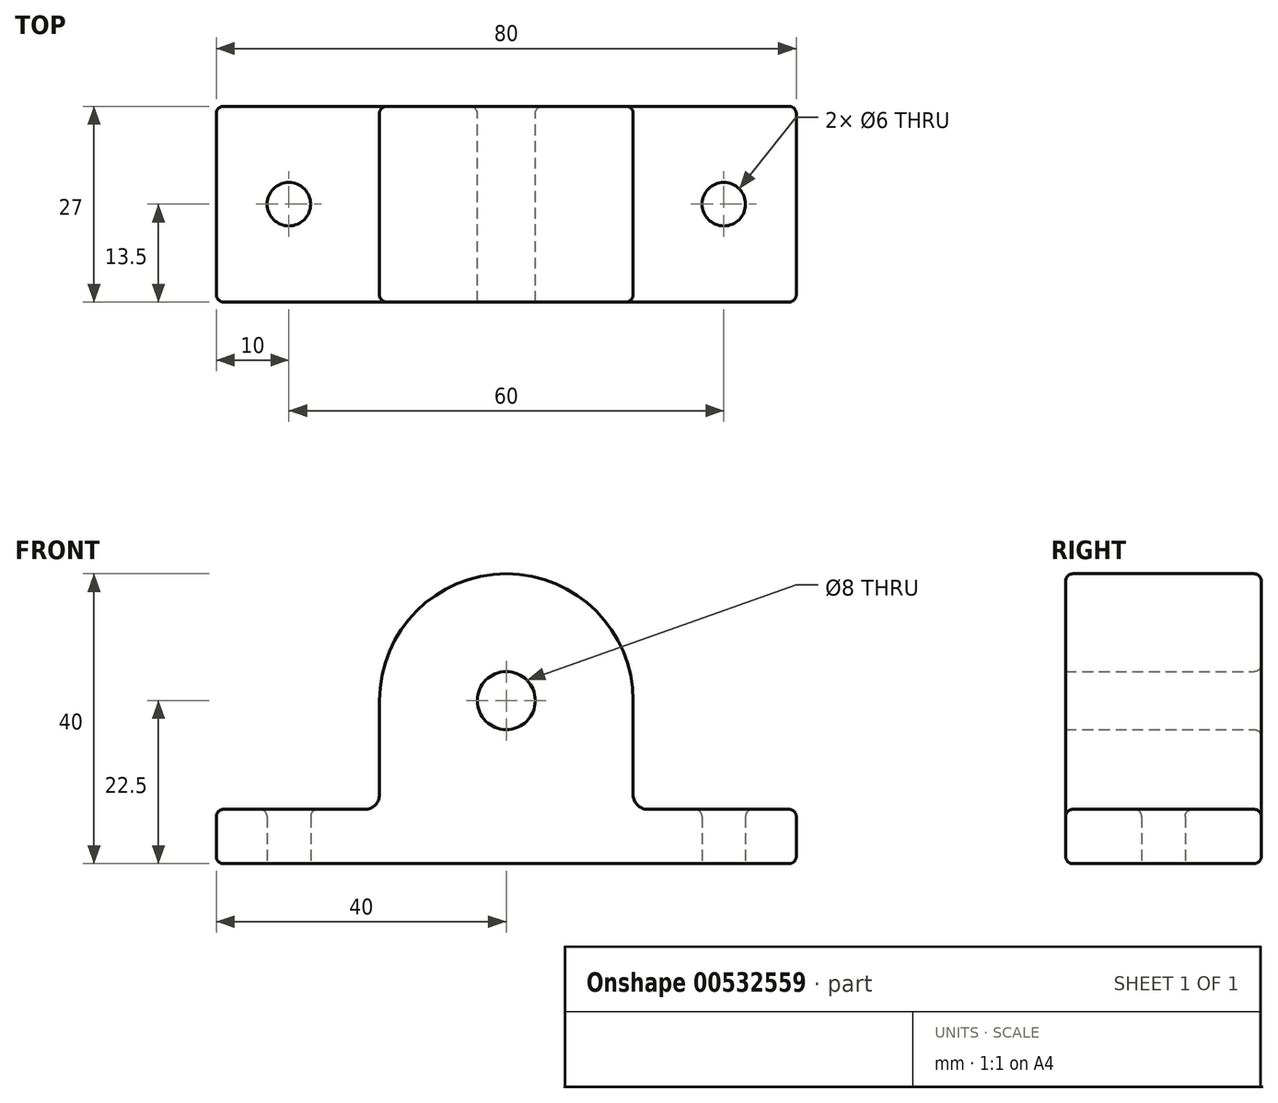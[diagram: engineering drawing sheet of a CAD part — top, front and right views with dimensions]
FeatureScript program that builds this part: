
annotation { "Feature Type Name" : "Feature", "Feature Type Description" : "" }
export const myFeature = defineFeature(function(context is Context, id is Id, definition is map)
    precondition{}
    {
        {
            var Q0;
            Q0=qCreatedBy(makeId("Top.planeOp"),FACE);
            var sketch = newSketch(context, id + "F0", { "sketchPlane" : qUnion([Q0])});
            skLineSegment(sketch, "E0.bottom", {"start": v(-40, 13.5) * mm, "end": v(40, 13.5) * mm});
            skLineSegment(sketch, "E0.top", {"start": v(-40, -13.5) * mm, "end": v(40, -13.5) * mm});
            skLineSegment(sketch, "E0.left", {"start": v(-40, 13.5) * mm, "end": v(-40, -13.5) * mm});
            skLineSegment(sketch, "E0.right", {"start": v(40, 13.5) * mm, "end": v(40, -13.5) * mm});
            skPoint(sketch, "E1", {"position": v(0, 13.5) * mm});
            skPoint(sketch, "E2", {"position": v(40, 0) * mm});
            skCircle(sketch, "E3", {"center": v(-30, 0) * mm, "radius": 3 * mm});
            skCircle(sketch, "E4", {"center": v(30, 0) * mm, "radius": 3 * mm});
            skSolve(sketch);
        }
        {
            var Q0;
            Q0=makeQuery(id+"F0.imprint","IMPRINT",FACE,{"disambiguationData":[TD([[makeQuery(id+"F0.imprint","IMPRINT",EDGE,{"derivedFrom":sQuery(id+"F0.wireOp",EDGE,"E0.bottom")}),-1.0]])]});
            extrude(context, id + "F1", {"entities" : qUnion([Q0]), "depth" : 7.5 * mm, "offsetDistance" : 25 * mm});
        }
        {
            var Q0;
            Q0=qCreatedBy(makeId("Front.planeOp"),FACE);
            var sketch = newSketch(context, id + "F2", { "sketchPlane" : qUnion([Q0])});
            skLineSegment(sketch, "E5", {"start": v(0, 0) * mm, "end": v(0, 40) * mm, "construction": true});
            skArc(sketch, "E6", {"start": v(17.5, 22.5) * mm, "mid": v(0, 40) * mm, "end": v(-17.5, 22.5) * mm});
            skLineSegment(sketch, "E7", {"start": v(0, 22.5) * mm, "end": v(-27.53, 22.5) * mm, "construction": true});
            skLineSegment(sketch, "E8", {"start": v(0, 22.5) * mm, "end": v(26.65, 22.5) * mm, "construction": true});
            skLineSegment(sketch, "E9", {"start": v(-17.5, 22.5) * mm, "end": v(-17.5, 2.5) * mm});
            skLineSegment(sketch, "E10", {"start": v(-17.5, 2.5) * mm, "end": v(17.5, 2.5) * mm});
            skLineSegment(sketch, "E11", {"start": v(17.5, 2.5) * mm, "end": v(17.5, 22.5) * mm});
            skCircle(sketch, "E12", {"center": v(0, 22.5) * mm, "radius": 4 * mm});
            skSolve(sketch);
        }
        {
            var Q0;
            Q0=makeQuery(id+"F2.imprint","IMPRINT",FACE,{"disambiguationData":[TD([[makeQuery(id+"F2.imprint","IMPRINT",EDGE,{"derivedFrom":sQuery(id+"F2.wireOp",EDGE,"E6")}),1.0]])]});
            extrude(context, id + "F3", {"entities" : qUnion([Q0]), "operationType" : NewBodyOperationType.ADD, "endBound" : BoundingType.SYMMETRIC, "depth" : 27 * mm, "offsetDistance" : 25 * mm});
        }
        {
            var Q0;
            Q0=makeQuery(id+"F3.boolean.opBoolean","INTERSECT",EDGE,{"derivedFrom":[makeQuery(id+"F1.opExtrude","CAP_FACE",FACE,{"disambiguationData":[OSD([sQuery(id+"F0.wireOp",EDGE,"E0.bottom"),sQuery(id+"F0.wireOp",EDGE,"E0.top"),sQuery(id+"F0.wireOp",EDGE,"E0.left"),sQuery(id+"F0.wireOp",EDGE,"E0.right"),sQuery(id+"F0.wireOp",EDGE,"E3"),sQuery(id+"F0.wireOp",EDGE,"E4")])],"isStart":false}),makeQuery(id+"F3.opExtrude","SWEPT_FACE",FACE,{"disambiguationData":[OSD([sQuery(id+"F2.wireOp",EDGE,"E11")])]})]});
            var Q1;
            Q1=makeQuery(id+"F3.boolean.opBoolean","INTERSECT",EDGE,{"derivedFrom":[makeQuery(id+"F1.opExtrude","CAP_FACE",FACE,{"disambiguationData":[OSD([sQuery(id+"F0.wireOp",EDGE,"E0.bottom"),sQuery(id+"F0.wireOp",EDGE,"E0.top"),sQuery(id+"F0.wireOp",EDGE,"E0.left"),sQuery(id+"F0.wireOp",EDGE,"E0.right"),sQuery(id+"F0.wireOp",EDGE,"E3"),sQuery(id+"F0.wireOp",EDGE,"E4")])],"isStart":false}),makeQuery(id+"F3.opExtrude","SWEPT_FACE",FACE,{"disambiguationData":[OSD([sQuery(id+"F2.wireOp",EDGE,"E9")])]})]});
            fillet(context, id + "F4", {"entities" : qUnion([Q0, Q1]), "radius" : 2 * mm, "tangentPropagation" : true, "allowEdgeOverflow" : false});
        }
        {
            var Q0;
            Q0=makeQuery(id+"F1.opExtrude","SWEPT_EDGE",EDGE,{"disambiguationData":[OSD([sQuery(id+"F0.wireOp",EDGE,"E0.top"),sQuery(id+"F0.wireOp",EDGE,"E0.left")])]});
            var Q1;
            Q1=makeQuery(id+"F1.opExtrude","SWEPT_EDGE",EDGE,{"disambiguationData":[OSD([sQuery(id+"F0.wireOp",EDGE,"E0.bottom"),sQuery(id+"F0.wireOp",EDGE,"E0.left")])]});
            var Q2;
            Q2=makeQuery(id+"F1.opExtrude","SWEPT_EDGE",EDGE,{"disambiguationData":[OSD([sQuery(id+"F0.wireOp",EDGE,"E0.top"),sQuery(id+"F0.wireOp",EDGE,"E0.right")])]});
            var Q3;
            Q3=makeQuery(id+"F1.opExtrude","SWEPT_EDGE",EDGE,{"disambiguationData":[OSD([sQuery(id+"F0.wireOp",EDGE,"E0.bottom"),sQuery(id+"F0.wireOp",EDGE,"E0.right")])]});
            fillet(context, id + "F5", {"entities" : qUnion([Q0, Q1, Q2, Q3]), "radius" : 1 * mm, "tangentPropagation" : true, "allowEdgeOverflow" : false});
        }
        {
            var Q0;
            {var subQ0=sQuery(id+"F0.wireOp",EDGE,"E3");var subQ1=sQuery(id+"F0.wireOp",EDGE,"E0.left");var subQ2=sQuery(id+"F0.wireOp",EDGE,"E0.top");var subQ3=sQuery(id+"F0.wireOp",EDGE,"E0.bottom");Q0=makeQuery(id+"F3.boolean.opBoolean","SPLIT",FACE,{"disambiguationData":[TD([makeQuery(id+"F1.opExtrude","SWEPT_FACE",FACE,{"disambiguationData":[OSD([subQ1])]})])],"derivedFrom":makeQuery(id+"F1.opExtrude","CAP_FACE",FACE,{"disambiguationData":[OSD([subQ3,subQ2,subQ1,sQuery(id+"F0.wireOp",EDGE,"E0.right"),subQ0,sQuery(id+"F0.wireOp",EDGE,"E4")])],"isStart":false})});}
            var Q1;
            Q1=makeQuery(id+"F4.opFillet","BLEND_FACE",FACE,{"disambiguationData":[OSD([sQuery(id+"F0.wireOp",EDGE,"E0.bottom"),sQuery(id+"F0.wireOp",EDGE,"E0.top"),sQuery(id+"F0.wireOp",EDGE,"E0.left"),sQuery(id+"F0.wireOp",EDGE,"E0.right"),sQuery(id+"F0.wireOp",EDGE,"E3"),sQuery(id+"F0.wireOp",EDGE,"E4"),sQuery(id+"F2.wireOp",EDGE,"E9")])]});
            var Q2;
            Q2=makeQuery(id+"F3.opExtrude","SWEPT_FACE",FACE,{"disambiguationData":[OSD([sQuery(id+"F2.wireOp",EDGE,"E9")])]});
            var Q3;
            Q3=makeQuery(id+"F3.opExtrude","SWEPT_FACE",FACE,{"disambiguationData":[OSD([sQuery(id+"F2.wireOp",EDGE,"E6")])]});
            var Q4;
            Q4=makeQuery(id+"F3.opExtrude","SWEPT_FACE",FACE,{"disambiguationData":[OSD([sQuery(id+"F2.wireOp",EDGE,"E11")])]});
            var Q5;
            Q5=makeQuery(id+"F3.boolean.opBoolean","MERGE",FACE,{"derivedFrom":[makeQuery(id+"F1.opExtrude","SWEPT_FACE",FACE,{"disambiguationData":[OSD([sQuery(id+"F0.wireOp",EDGE,"E0.bottom")])]}),makeQuery(id+"F3.opExtrude","CAP_FACE",FACE,{"disambiguationData":[OSD([sQuery(id+"F2.wireOp",EDGE,"E6"),sQuery(id+"F2.wireOp",EDGE,"E9"),sQuery(id+"F2.wireOp",EDGE,"E10"),sQuery(id+"F2.wireOp",EDGE,"E11")])],"isStart":true})]});
            var Q6;
            Q6=makeQuery(id+"F4.opFillet","BLEND_FACE",FACE,{"disambiguationData":[OSD([sQuery(id+"F0.wireOp",EDGE,"E0.bottom"),sQuery(id+"F0.wireOp",EDGE,"E0.top"),sQuery(id+"F0.wireOp",EDGE,"E0.left"),sQuery(id+"F0.wireOp",EDGE,"E0.right"),sQuery(id+"F0.wireOp",EDGE,"E3"),sQuery(id+"F0.wireOp",EDGE,"E4"),sQuery(id+"F2.wireOp",EDGE,"E11")])]});
            var Q7;
            {var subQ0=sQuery(id+"F0.wireOp",EDGE,"E4");var subQ1=sQuery(id+"F0.wireOp",EDGE,"E0.top");var subQ3=sQuery(id+"F0.wireOp",EDGE,"E0.right");var subQ4=sQuery(id+"F0.wireOp",EDGE,"E0.bottom");Q7=makeQuery(id+"F3.boolean.opBoolean","SPLIT",FACE,{"disambiguationData":[TD([makeQuery(id+"F1.opExtrude","SWEPT_FACE",FACE,{"disambiguationData":[OSD([subQ3])]})])],"derivedFrom":makeQuery(id+"F1.opExtrude","CAP_FACE",FACE,{"disambiguationData":[OSD([subQ4,subQ1,sQuery(id+"F0.wireOp",EDGE,"E0.left"),subQ3,sQuery(id+"F0.wireOp",EDGE,"E3"),subQ0])],"isStart":false})});}
            fillet(context, id + "F6", {"entities" : qUnion([Q0, Q1, Q2, Q3, Q4, Q5, Q6, Q7]), "radius" : 1 * mm, "tangentPropagation" : true, "allowEdgeOverflow" : false});
        }
    });
